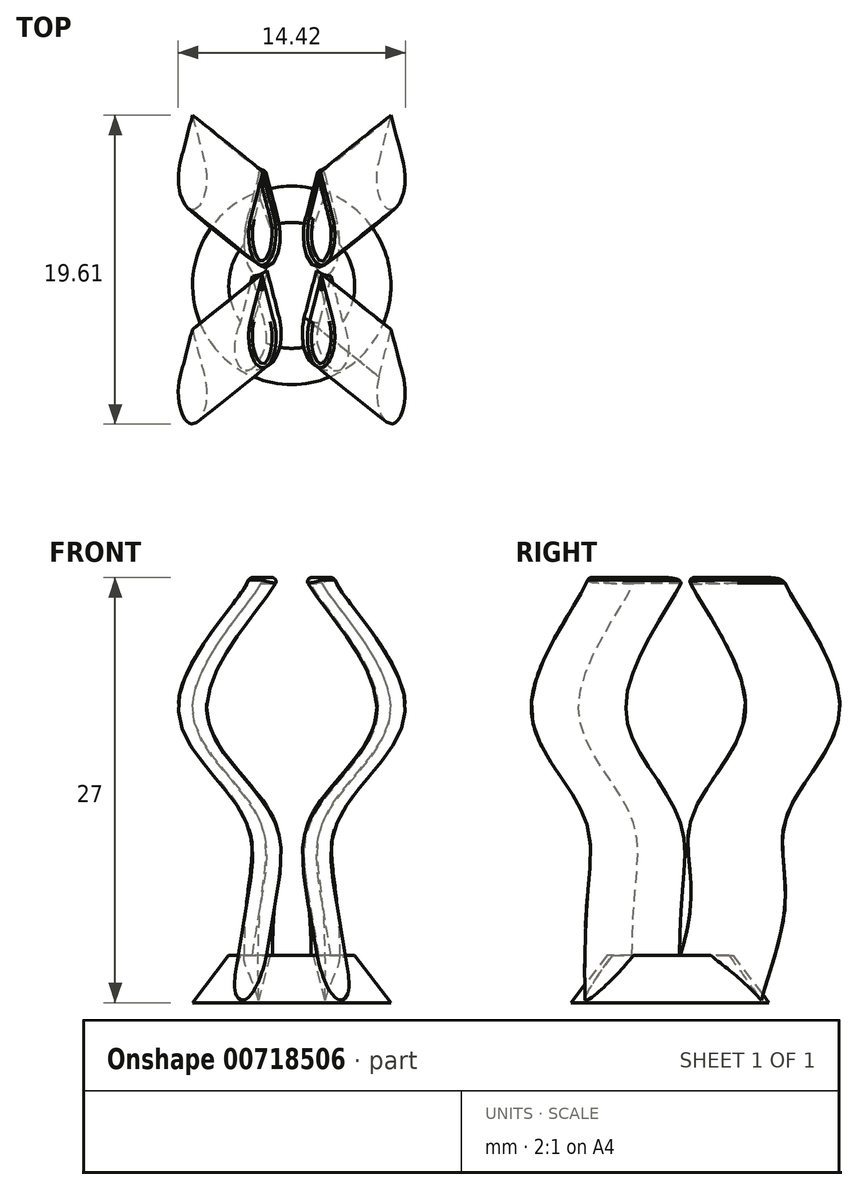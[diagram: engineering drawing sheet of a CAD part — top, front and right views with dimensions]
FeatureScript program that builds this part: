
annotation { "Feature Type Name" : "Feature", "Feature Type Description" : "" }
export const myFeature = defineFeature(function(context is Context, id is Id, definition is map)
    precondition{}
    {
        {
            var Q0;
            Q0=qCreatedBy(makeId("Top.planeOp"),FACE);
            var sketch = newSketch(context, id + "F0", { "sketchPlane" : qUnion([Q0])});
            skCircle(sketch, "E0", {"center": v(0, 0) * mm, "radius": 6.3 * mm});
            skSolve(sketch);
        }
        {
            assignVariable(context, id + "F1", {"variableType" : VariableType.LENGTH, "name" : "BaseHeight", "lengthValue" : 3 * mm});
        }
        {
            var Q0;
            Q0=qCreatedBy(makeId("Top.planeOp"),FACE);
            cPlane(context, id + "F2", {"entities" : qUnion([Q0]), "cplaneType" : CPlaneType.OFFSET, "offset" : getVariable(context, 'BaseHeight'), "width" : 150 * mm, "height" : 150 * mm});
        }
        {
            var Q0;
            Q0=qCreatedBy(id+"F2.planeOp",FACE);
            var sketch = newSketch(context, id + "F3", { "sketchPlane" : qUnion([Q0])});
            skCircle(sketch, "E1", {"center": v(0, 0) * mm, "radius": 4 * mm});
            skSolve(sketch);
        }
        {
            assignVariable(context, id + "F4", {"variableType" : VariableType.LENGTH, "name" : "PostH1", "lengthValue" : 6 * mm});
        }
        {
            assignVariable(context, id + "F5", {"variableType" : VariableType.LENGTH, "name" : "PostH2", "lengthValue" : 11 * mm});
        }
        {
            assignVariable(context, id + "F6", {"variableType" : VariableType.LENGTH, "name" : "PostH3", "lengthValue" : 19 * mm});
        }
        {
            assignVariable(context, id + "F7", {"variableType" : VariableType.LENGTH, "name" : "PostH4", "lengthValue" : 27 * mm});
        }
        {
            var Q0;
            Q0=qCreatedBy(makeId("Top.planeOp"),FACE);
            cPlane(context, id + "F8", {"entities" : qUnion([Q0]), "cplaneType" : CPlaneType.OFFSET, "offset" : getVariable(context, 'PostH1'), "width" : 150 * mm, "height" : 150 * mm});
        }
        {
            var Q0;
            Q0=qCreatedBy(makeId("Top.planeOp"),FACE);
            cPlane(context, id + "F9", {"entities" : qUnion([Q0]), "cplaneType" : CPlaneType.OFFSET, "offset" : getVariable(context, 'PostH2'), "width" : 150 * mm, "height" : 150 * mm});
        }
        {
            var Q0;
            Q0=qCreatedBy(makeId("Top.planeOp"),FACE);
            cPlane(context, id + "F10", {"entities" : qUnion([Q0]), "cplaneType" : CPlaneType.OFFSET, "offset" : getVariable(context, 'PostH3'), "width" : 150 * mm, "height" : 150 * mm});
        }
        {
            var Q0;
            Q0=qCreatedBy(makeId("Top.planeOp"),FACE);
            cPlane(context, id + "F11", {"entities" : qUnion([Q0]), "cplaneType" : CPlaneType.OFFSET, "offset" : getVariable(context, 'PostH4'), "width" : 150 * mm, "height" : 150 * mm});
        }
        {
            var Q0;
            Q0=makeQuery(id+"F0.imprint","IMPRINT",FACE,{"disambiguationData":[TD([[makeQuery(id+"F0.imprint","IMPRINT",EDGE,{"derivedFrom":sQuery(id+"F0.wireOp",EDGE,"E0")}),1.0]])]});
            var Q1;
            Q1=makeQuery(id+"F3.imprint","IMPRINT",FACE,{"disambiguationData":[TD([[makeQuery(id+"F3.imprint","IMPRINT",EDGE,{"derivedFrom":sQuery(id+"F3.wireOp",EDGE,"E1")}),1.0]])]});
            loft(context, id + "F12", {"sheetProfilesArray" : [{ "sheetProfileEntities" : qUnion([Q0]) }, { "sheetProfileEntities" : qUnion([Q1]) }]});
        }
        {
            var Q0;
            Q0=qCreatedBy(makeId("Top.planeOp"),FACE);
            var sketch = newSketch(context, id + "F13", { "sketchPlane" : qUnion([Q0])});
            skEllipse(sketch, "E2", {"center": v(-2.1, 1.8) * mm, "majorRadius": 2 * mm, "minorRadius": 0.9 * mm, "majorAxis": v(0, 1)});
            skLineSegment(sketch, "E3", {"start": v(-2.88, 2.8) * mm, "end": v(-2.1, 5.8) * mm});
            skLineSegment(sketch, "E4", {"start": v(-2.1, 5.8) * mm, "end": v(-1.32, 2.8) * mm});
            skEllipse(sketch, "E5", {"center": v(2.1, 1.8) * mm, "majorRadius": 2 * mm, "minorRadius": 0.9 * mm, "majorAxis": v(0, 1)});
            skLineSegment(sketch, "E6", {"start": v(1.32, 2.8) * mm, "end": v(2.1, 5.8) * mm});
            skLineSegment(sketch, "E7", {"start": v(2.1, 5.8) * mm, "end": v(2.88, 2.8) * mm});
            skEllipse(sketch, "E8", {"center": v(-2.9, -3.4) * mm, "majorRadius": 2 * mm, "minorRadius": 0.9 * mm, "majorAxis": v(0, 1)});
            skLineSegment(sketch, "E9", {"start": v(-3.68, -2.4) * mm, "end": v(-2.9, 0.6) * mm});
            skLineSegment(sketch, "E10", {"start": v(-2.9, 0.6) * mm, "end": v(-2.12, -2.4) * mm});
            skEllipse(sketch, "E11", {"center": v(2.9, -3.4) * mm, "majorRadius": 2 * mm, "minorRadius": 0.9 * mm, "majorAxis": v(0, 1)});
            skLineSegment(sketch, "E12", {"start": v(2.12, -2.4) * mm, "end": v(2.9, 0.6) * mm});
            skLineSegment(sketch, "E13", {"start": v(2.9, 0.6) * mm, "end": v(3.68, -2.4) * mm});
            skSolve(sketch);
        }
        {
            var Q0;
            Q0=qCreatedBy(id+"F8.planeOp",FACE);
            var sketch = newSketch(context, id + "F14", { "sketchPlane" : qUnion([Q0])});
            skEllipse(sketch, "E14", {"center": v(-2, 3.3) * mm, "majorRadius": 2 * mm, "minorRadius": 0.9 * mm, "majorAxis": v(0, 1)});
            skLineSegment(sketch, "E15", {"start": v(-2.78, 4.3) * mm, "end": v(-2, 7.3) * mm});
            skLineSegment(sketch, "E16", {"start": v(-2, 7.3) * mm, "end": v(-1.22, 4.3) * mm});
            skEllipse(sketch, "E17", {"center": v(2, 3.3) * mm, "majorRadius": 2 * mm, "minorRadius": 0.9 * mm, "majorAxis": v(0, 1)});
            skLineSegment(sketch, "E18", {"start": v(1.22, 4.3) * mm, "end": v(2, 7.3) * mm});
            skLineSegment(sketch, "E19", {"start": v(2, 7.3) * mm, "end": v(2.78, 4.3) * mm});
            skEllipse(sketch, "E20", {"center": v(-2, -3.3) * mm, "majorRadius": 2 * mm, "minorRadius": 0.9 * mm, "majorAxis": v(0, 1)});
            skLineSegment(sketch, "E21", {"start": v(-2.78, -2.3) * mm, "end": v(-2, 0.7) * mm});
            skLineSegment(sketch, "E22", {"start": v(-2, 0.7) * mm, "end": v(-1.22, -2.3) * mm});
            skEllipse(sketch, "E23", {"center": v(2, -3.3) * mm, "majorRadius": 2 * mm, "minorRadius": 0.9 * mm, "majorAxis": v(0, 1)});
            skLineSegment(sketch, "E24", {"start": v(1.22, -2.3) * mm, "end": v(2, 0.7) * mm});
            skLineSegment(sketch, "E25", {"start": v(2, 0.7) * mm, "end": v(2.78, -2.3) * mm});
            skSolve(sketch);
        }
        {
            var Q0;
            Q0=qCreatedBy(id+"F9.planeOp",FACE);
            var sketch = newSketch(context, id + "F15", { "sketchPlane" : qUnion([Q0])});
            skEllipse(sketch, "E26", {"center": v(-1.8, 3.2) * mm, "majorRadius": 2 * mm, "minorRadius": 0.9 * mm, "majorAxis": v(0, 1)});
            skLineSegment(sketch, "E27", {"start": v(-2.58, 4.2) * mm, "end": v(-1.8, 7.2) * mm});
            skLineSegment(sketch, "E28", {"start": v(-1.8, 7.2) * mm, "end": v(-1.02, 4.2) * mm});
            skEllipse(sketch, "E29", {"center": v(1.8, 3.2) * mm, "majorRadius": 2 * mm, "minorRadius": 0.9 * mm, "majorAxis": v(0, 1)});
            skLineSegment(sketch, "E30", {"start": v(1.02, 4.2) * mm, "end": v(1.8, 7.2) * mm});
            skLineSegment(sketch, "E31", {"start": v(1.8, 7.2) * mm, "end": v(2.58, 4.2) * mm});
            skEllipse(sketch, "E32", {"center": v(-1.8, -3.2) * mm, "majorRadius": 2 * mm, "minorRadius": 0.9 * mm, "majorAxis": v(0, 1)});
            skLineSegment(sketch, "E33", {"start": v(-2.58, -2.2) * mm, "end": v(-1.8, 0.8) * mm});
            skLineSegment(sketch, "E34", {"start": v(-1.8, 0.8) * mm, "end": v(-1.02, -2.2) * mm});
            skEllipse(sketch, "E35", {"center": v(1.8, -3.2) * mm, "majorRadius": 2 * mm, "minorRadius": 0.9 * mm, "majorAxis": v(0, 1)});
            skLineSegment(sketch, "E36", {"start": v(1.02, -2.2) * mm, "end": v(1.8, 0.8) * mm});
            skLineSegment(sketch, "E37", {"start": v(1.8, 0.8) * mm, "end": v(2.58, -2.2) * mm});
            skSolve(sketch);
        }
        {
            var Q0;
            Q0=qCreatedBy(id+"F10.planeOp",FACE);
            var sketch = newSketch(context, id + "F16", { "sketchPlane" : qUnion([Q0])});
            skEllipse(sketch, "E38", {"center": v(-6.3, 6.8) * mm, "majorRadius": 2 * mm, "minorRadius": 0.9 * mm, "majorAxis": v(0, 1)});
            skLineSegment(sketch, "E39", {"start": v(-7.08, 7.8) * mm, "end": v(-6.3, 10.8) * mm});
            skLineSegment(sketch, "E40", {"start": v(-6.3, 10.8) * mm, "end": v(-5.52, 7.8) * mm});
            skEllipse(sketch, "E41", {"center": v(6.3, 6.8) * mm, "majorRadius": 2 * mm, "minorRadius": 0.9 * mm, "majorAxis": v(0, 1)});
            skLineSegment(sketch, "E42", {"start": v(5.52, 7.8) * mm, "end": v(6.3, 10.8) * mm});
            skLineSegment(sketch, "E43", {"start": v(6.3, 10.8) * mm, "end": v(7.08, 7.8) * mm});
            skEllipse(sketch, "E44", {"center": v(-6.3, -6.8) * mm, "majorRadius": 2 * mm, "minorRadius": 0.9 * mm, "majorAxis": v(0, 1)});
            skLineSegment(sketch, "E45", {"start": v(-7.08, -5.8) * mm, "end": v(-6.3, -2.8) * mm});
            skLineSegment(sketch, "E46", {"start": v(-6.3, -2.8) * mm, "end": v(-5.52, -5.8) * mm});
            skEllipse(sketch, "E47", {"center": v(6.3, -6.8) * mm, "majorRadius": 2 * mm, "minorRadius": 0.9 * mm, "majorAxis": v(0, 1)});
            skLineSegment(sketch, "E48", {"start": v(5.52, -5.8) * mm, "end": v(6.3, -2.8) * mm});
            skLineSegment(sketch, "E49", {"start": v(6.3, -2.8) * mm, "end": v(7.08, -5.8) * mm});
            skSolve(sketch);
        }
        {
            var Q0;
            Q0=qCreatedBy(id+"F11.planeOp",FACE);
            var sketch = newSketch(context, id + "F17", { "sketchPlane" : qUnion([Q0])});
            skEllipse(sketch, "E50", {"center": v(-1.8, 3.2) * mm, "majorRadius": 2 * mm, "minorRadius": 0.9 * mm, "majorAxis": v(0, 1)});
            skLineSegment(sketch, "E51", {"start": v(-2.58, 4.2) * mm, "end": v(-1.8, 7.2) * mm});
            skLineSegment(sketch, "E52", {"start": v(-1.8, 7.2) * mm, "end": v(-1.02, 4.2) * mm});
            skEllipse(sketch, "E53", {"center": v(1.8, 3.2) * mm, "majorRadius": 2 * mm, "minorRadius": 0.9 * mm, "majorAxis": v(0, 1)});
            skLineSegment(sketch, "E54", {"start": v(1.02, 4.2) * mm, "end": v(1.8, 7.2) * mm});
            skLineSegment(sketch, "E55", {"start": v(1.8, 7.2) * mm, "end": v(2.58, 4.2) * mm});
            skEllipse(sketch, "E56", {"center": v(-1.8, -3.2) * mm, "majorRadius": 2 * mm, "minorRadius": 0.9 * mm, "majorAxis": v(0, 1)});
            skLineSegment(sketch, "E57", {"start": v(-2.58, -2.2) * mm, "end": v(-1.8, 0.8) * mm});
            skLineSegment(sketch, "E58", {"start": v(-1.8, 0.8) * mm, "end": v(-1.02, -2.2) * mm});
            skEllipse(sketch, "E59", {"center": v(1.8, -3.2) * mm, "majorRadius": 2 * mm, "minorRadius": 0.9 * mm, "majorAxis": v(0, 1)});
            skLineSegment(sketch, "E60", {"start": v(1.02, -2.2) * mm, "end": v(1.8, 0.8) * mm});
            skLineSegment(sketch, "E61", {"start": v(1.8, 0.8) * mm, "end": v(2.58, -2.2) * mm});
            skSolve(sketch);
        }
        {
            assignVariable(context, id + "F18", {"variableType" : VariableType.NUMBER, "name" : "Loft1", "numberValue" : 0.3});
        }
        {
            var Q0;
            {var subQ0=sQuery(id+"F13.wireOp",EDGE,"E5");var subQ1=makeQuery(id+"F13.imprint","INTERSECT",VERTEX,{"derivedFrom":[subQ0,sQuery(id+"F13.wireOp",EDGE,"E6")]});Q0=makeQuery(id+"F13.imprint","IMPRINT",FACE,{"disambiguationData":[TD([[makeQuery(id+"F13.imprint","IMPRINT",EDGE,{"disambiguationData":[TD([[subQ1,-1.0]])],"derivedFrom":subQ0}),1.0]])]});}
            var Q1;
            {var subQ0=sQuery(id+"F13.wireOp",EDGE,"E6");Q1=makeQuery(id+"F13.imprint","IMPRINT",FACE,{"disambiguationData":[TD([[makeQuery(id+"F13.imprint","IMPRINT",EDGE,{"derivedFrom":subQ0}),-1.0]])]});}
            var Q2;
            {var subQ0=sQuery(id+"F14.wireOp",EDGE,"E17");var subQ1=makeQuery(id+"F14.imprint","INTERSECT",VERTEX,{"derivedFrom":[subQ0,sQuery(id+"F14.wireOp",EDGE,"E18")]});Q2=makeQuery(id+"F14.imprint","IMPRINT",FACE,{"disambiguationData":[TD([[makeQuery(id+"F14.imprint","IMPRINT",EDGE,{"disambiguationData":[TD([[subQ1,-1.0]])],"derivedFrom":subQ0}),1.0]])]});}
            var Q3;
            {var subQ0=sQuery(id+"F14.wireOp",EDGE,"E18");Q3=makeQuery(id+"F14.imprint","IMPRINT",FACE,{"disambiguationData":[TD([[makeQuery(id+"F14.imprint","IMPRINT",EDGE,{"derivedFrom":subQ0}),-1.0]])]});}
            var Q4;
            {var subQ0=sQuery(id+"F15.wireOp",EDGE,"E29");var subQ1=makeQuery(id+"F15.imprint","INTERSECT",VERTEX,{"derivedFrom":[subQ0,sQuery(id+"F15.wireOp",EDGE,"E30")]});Q4=makeQuery(id+"F15.imprint","IMPRINT",FACE,{"disambiguationData":[TD([[makeQuery(id+"F15.imprint","IMPRINT",EDGE,{"disambiguationData":[TD([[subQ1,-1.0]])],"derivedFrom":subQ0}),1.0]])]});}
            var Q5;
            {var subQ0=sQuery(id+"F15.wireOp",EDGE,"E30");Q5=makeQuery(id+"F15.imprint","IMPRINT",FACE,{"disambiguationData":[TD([[makeQuery(id+"F15.imprint","IMPRINT",EDGE,{"derivedFrom":subQ0}),-1.0]])]});}
            var Q6;
            {var subQ0=sQuery(id+"F16.wireOp",EDGE,"E41");var subQ1=makeQuery(id+"F16.imprint","INTERSECT",VERTEX,{"derivedFrom":[subQ0,sQuery(id+"F16.wireOp",EDGE,"E42")]});Q6=makeQuery(id+"F16.imprint","IMPRINT",FACE,{"disambiguationData":[TD([[makeQuery(id+"F16.imprint","IMPRINT",EDGE,{"disambiguationData":[TD([[subQ1,-1.0]])],"derivedFrom":subQ0}),1.0]])]});}
            var Q7;
            {var subQ0=sQuery(id+"F16.wireOp",EDGE,"E42");Q7=makeQuery(id+"F16.imprint","IMPRINT",FACE,{"disambiguationData":[TD([[makeQuery(id+"F16.imprint","IMPRINT",EDGE,{"derivedFrom":subQ0}),-1.0]])]});}
            var Q8;
            {var subQ0=sQuery(id+"F17.wireOp",EDGE,"E53");var subQ1=makeQuery(id+"F17.imprint","INTERSECT",VERTEX,{"derivedFrom":[subQ0,sQuery(id+"F17.wireOp",EDGE,"E54")]});Q8=makeQuery(id+"F17.imprint","IMPRINT",FACE,{"disambiguationData":[TD([[makeQuery(id+"F17.imprint","IMPRINT",EDGE,{"disambiguationData":[TD([[subQ1,-1.0]])],"derivedFrom":subQ0}),1.0]])]});}
            var Q9;
            {var subQ0=sQuery(id+"F17.wireOp",EDGE,"E54");Q9=makeQuery(id+"F17.imprint","IMPRINT",FACE,{"disambiguationData":[TD([[makeQuery(id+"F17.imprint","IMPRINT",EDGE,{"derivedFrom":subQ0}),-1.0]])]});}
            loft(context, id + "F19", {"operationType" : NewBodyOperationType.ADD, "sheetProfilesArray" : [{ "sheetProfileEntities" : qUnion([Q0, Q1]) }, { "sheetProfileEntities" : qUnion([Q2, Q3]) }, { "sheetProfileEntities" : qUnion([Q4, Q5]) }, { "sheetProfileEntities" : qUnion([Q6, Q7]) }, { "sheetProfileEntities" : qUnion([Q8, Q9]) }], "startCondition" : LoftEndDerivativeType.NORMAL_TO_PROFILE, "startMagnitude" : getVariable(context, 'Loft1'), "endCondition" : LoftEndDerivativeType.NORMAL_TO_PROFILE, "endMagnitude" : getVariable(context, 'Loft1')});
        }
        {
            var Q0;
            {var subQ0=sQuery(id+"F13.wireOp",EDGE,"E3");Q0=makeQuery(id+"F13.imprint","IMPRINT",FACE,{"disambiguationData":[TD([[makeQuery(id+"F13.imprint","IMPRINT",EDGE,{"derivedFrom":subQ0}),-1.0]])]});}
            var Q1;
            {var subQ0=sQuery(id+"F13.wireOp",EDGE,"E2");var subQ1=makeQuery(id+"F13.imprint","INTERSECT",VERTEX,{"derivedFrom":[subQ0,sQuery(id+"F13.wireOp",EDGE,"E3")]});Q1=makeQuery(id+"F13.imprint","IMPRINT",FACE,{"disambiguationData":[TD([[makeQuery(id+"F13.imprint","IMPRINT",EDGE,{"disambiguationData":[TD([[subQ1,-1.0]])],"derivedFrom":subQ0}),1.0]])]});}
            var Q2;
            {var subQ0=sQuery(id+"F14.wireOp",EDGE,"E15");Q2=makeQuery(id+"F14.imprint","IMPRINT",FACE,{"disambiguationData":[TD([[makeQuery(id+"F14.imprint","IMPRINT",EDGE,{"derivedFrom":subQ0}),-1.0]])]});}
            var Q3;
            {var subQ0=sQuery(id+"F14.wireOp",EDGE,"E14");var subQ1=makeQuery(id+"F14.imprint","INTERSECT",VERTEX,{"derivedFrom":[subQ0,sQuery(id+"F14.wireOp",EDGE,"E15")]});Q3=makeQuery(id+"F14.imprint","IMPRINT",FACE,{"disambiguationData":[TD([[makeQuery(id+"F14.imprint","IMPRINT",EDGE,{"disambiguationData":[TD([[subQ1,-1.0]])],"derivedFrom":subQ0}),1.0]])]});}
            var Q4;
            {var subQ0=sQuery(id+"F15.wireOp",EDGE,"E26");var subQ1=makeQuery(id+"F15.imprint","INTERSECT",VERTEX,{"derivedFrom":[subQ0,sQuery(id+"F15.wireOp",EDGE,"E27")]});Q4=makeQuery(id+"F15.imprint","IMPRINT",FACE,{"disambiguationData":[TD([[makeQuery(id+"F15.imprint","IMPRINT",EDGE,{"disambiguationData":[TD([[subQ1,-1.0]])],"derivedFrom":subQ0}),1.0]])]});}
            var Q5;
            {var subQ0=sQuery(id+"F15.wireOp",EDGE,"E27");Q5=makeQuery(id+"F15.imprint","IMPRINT",FACE,{"disambiguationData":[TD([[makeQuery(id+"F15.imprint","IMPRINT",EDGE,{"derivedFrom":subQ0}),-1.0]])]});}
            var Q6;
            {var subQ0=sQuery(id+"F16.wireOp",EDGE,"E38");var subQ1=makeQuery(id+"F16.imprint","INTERSECT",VERTEX,{"derivedFrom":[subQ0,sQuery(id+"F16.wireOp",EDGE,"E39")]});Q6=makeQuery(id+"F16.imprint","IMPRINT",FACE,{"disambiguationData":[TD([[makeQuery(id+"F16.imprint","IMPRINT",EDGE,{"disambiguationData":[TD([[subQ1,-1.0]])],"derivedFrom":subQ0}),1.0]])]});}
            var Q7;
            {var subQ0=sQuery(id+"F16.wireOp",EDGE,"E39");Q7=makeQuery(id+"F16.imprint","IMPRINT",FACE,{"disambiguationData":[TD([[makeQuery(id+"F16.imprint","IMPRINT",EDGE,{"derivedFrom":subQ0}),-1.0]])]});}
            var Q8;
            {var subQ0=sQuery(id+"F17.wireOp",EDGE,"E50");var subQ1=makeQuery(id+"F17.imprint","INTERSECT",VERTEX,{"derivedFrom":[subQ0,sQuery(id+"F17.wireOp",EDGE,"E51")]});Q8=makeQuery(id+"F17.imprint","IMPRINT",FACE,{"disambiguationData":[TD([[makeQuery(id+"F17.imprint","IMPRINT",EDGE,{"disambiguationData":[TD([[subQ1,-1.0]])],"derivedFrom":subQ0}),1.0]])]});}
            var Q9;
            {var subQ0=sQuery(id+"F17.wireOp",EDGE,"E51");Q9=makeQuery(id+"F17.imprint","IMPRINT",FACE,{"disambiguationData":[TD([[makeQuery(id+"F17.imprint","IMPRINT",EDGE,{"derivedFrom":subQ0}),-1.0]])]});}
            loft(context, id + "F20", {"operationType" : NewBodyOperationType.ADD, "sheetProfilesArray" : [{ "sheetProfileEntities" : qUnion([Q0, Q1]) }, { "sheetProfileEntities" : qUnion([Q2, Q3]) }, { "sheetProfileEntities" : qUnion([Q4, Q5]) }, { "sheetProfileEntities" : qUnion([Q6, Q7]) }, { "sheetProfileEntities" : qUnion([Q8, Q9]) }], "startCondition" : LoftEndDerivativeType.NORMAL_TO_PROFILE, "startMagnitude" : getVariable(context, 'Loft1'), "endCondition" : LoftEndDerivativeType.NORMAL_TO_PROFILE, "endMagnitude" : getVariable(context, 'Loft1')});
        }
        {
            var Q0;
            {var subQ0=sQuery(id+"F13.wireOp",EDGE,"E9");Q0=makeQuery(id+"F13.imprint","IMPRINT",FACE,{"disambiguationData":[TD([[makeQuery(id+"F13.imprint","IMPRINT",EDGE,{"derivedFrom":subQ0}),-1.0]])]});}
            var Q1;
            {var subQ0=sQuery(id+"F13.wireOp",EDGE,"E8");var subQ1=makeQuery(id+"F13.imprint","INTERSECT",VERTEX,{"derivedFrom":[subQ0,sQuery(id+"F13.wireOp",EDGE,"E9")]});Q1=makeQuery(id+"F13.imprint","IMPRINT",FACE,{"disambiguationData":[TD([[makeQuery(id+"F13.imprint","IMPRINT",EDGE,{"disambiguationData":[TD([[subQ1,-1.0]])],"derivedFrom":subQ0}),1.0]])]});}
            var Q2;
            {var subQ0=sQuery(id+"F14.wireOp",EDGE,"E21");Q2=makeQuery(id+"F14.imprint","IMPRINT",FACE,{"disambiguationData":[TD([[makeQuery(id+"F14.imprint","IMPRINT",EDGE,{"derivedFrom":subQ0}),-1.0]])]});}
            var Q3;
            {var subQ0=sQuery(id+"F14.wireOp",EDGE,"E20");var subQ1=makeQuery(id+"F14.imprint","INTERSECT",VERTEX,{"derivedFrom":[subQ0,sQuery(id+"F14.wireOp",EDGE,"E21")]});Q3=makeQuery(id+"F14.imprint","IMPRINT",FACE,{"disambiguationData":[TD([[makeQuery(id+"F14.imprint","IMPRINT",EDGE,{"disambiguationData":[TD([[subQ1,-1.0]])],"derivedFrom":subQ0}),1.0]])]});}
            var Q4;
            {var subQ0=sQuery(id+"F15.wireOp",EDGE,"E32");var subQ1=makeQuery(id+"F15.imprint","INTERSECT",VERTEX,{"derivedFrom":[subQ0,sQuery(id+"F15.wireOp",EDGE,"E33")]});Q4=makeQuery(id+"F15.imprint","IMPRINT",FACE,{"disambiguationData":[TD([[makeQuery(id+"F15.imprint","IMPRINT",EDGE,{"disambiguationData":[TD([[subQ1,-1.0]])],"derivedFrom":subQ0}),1.0]])]});}
            var Q5;
            {var subQ0=sQuery(id+"F15.wireOp",EDGE,"E33");Q5=makeQuery(id+"F15.imprint","IMPRINT",FACE,{"disambiguationData":[TD([[makeQuery(id+"F15.imprint","IMPRINT",EDGE,{"derivedFrom":subQ0}),-1.0]])]});}
            var Q6;
            {var subQ0=sQuery(id+"F16.wireOp",EDGE,"E44");var subQ1=makeQuery(id+"F16.imprint","INTERSECT",VERTEX,{"derivedFrom":[subQ0,sQuery(id+"F16.wireOp",EDGE,"E45")]});Q6=makeQuery(id+"F16.imprint","IMPRINT",FACE,{"disambiguationData":[TD([[makeQuery(id+"F16.imprint","IMPRINT",EDGE,{"disambiguationData":[TD([[subQ1,-1.0]])],"derivedFrom":subQ0}),1.0]])]});}
            var Q7;
            {var subQ0=sQuery(id+"F16.wireOp",EDGE,"E45");Q7=makeQuery(id+"F16.imprint","IMPRINT",FACE,{"disambiguationData":[TD([[makeQuery(id+"F16.imprint","IMPRINT",EDGE,{"derivedFrom":subQ0}),-1.0]])]});}
            var Q8;
            {var subQ0=sQuery(id+"F17.wireOp",EDGE,"E56");var subQ1=makeQuery(id+"F17.imprint","INTERSECT",VERTEX,{"derivedFrom":[subQ0,sQuery(id+"F17.wireOp",EDGE,"E57")]});Q8=makeQuery(id+"F17.imprint","IMPRINT",FACE,{"disambiguationData":[TD([[makeQuery(id+"F17.imprint","IMPRINT",EDGE,{"disambiguationData":[TD([[subQ1,-1.0]])],"derivedFrom":subQ0}),1.0]])]});}
            var Q9;
            {var subQ0=sQuery(id+"F17.wireOp",EDGE,"E57");Q9=makeQuery(id+"F17.imprint","IMPRINT",FACE,{"disambiguationData":[TD([[makeQuery(id+"F17.imprint","IMPRINT",EDGE,{"derivedFrom":subQ0}),-1.0]])]});}
            loft(context, id + "F21", {"operationType" : NewBodyOperationType.ADD, "sheetProfilesArray" : [{ "sheetProfileEntities" : qUnion([Q0, Q1]) }, { "sheetProfileEntities" : qUnion([Q2, Q3]) }, { "sheetProfileEntities" : qUnion([Q4, Q5]) }, { "sheetProfileEntities" : qUnion([Q6, Q7]) }, { "sheetProfileEntities" : qUnion([Q8, Q9]) }], "startCondition" : LoftEndDerivativeType.NORMAL_TO_PROFILE, "startMagnitude" : getVariable(context, 'Loft1'), "endCondition" : LoftEndDerivativeType.NORMAL_TO_PROFILE, "endMagnitude" : getVariable(context, 'Loft1')});
        }
        {
            var Q0;
            {var subQ0=sQuery(id+"F13.wireOp",EDGE,"E11");var subQ1=makeQuery(id+"F13.imprint","INTERSECT",VERTEX,{"derivedFrom":[subQ0,sQuery(id+"F13.wireOp",EDGE,"E12")]});Q0=makeQuery(id+"F13.imprint","IMPRINT",FACE,{"disambiguationData":[TD([[makeQuery(id+"F13.imprint","IMPRINT",EDGE,{"disambiguationData":[TD([[subQ1,-1.0]])],"derivedFrom":subQ0}),1.0]])]});}
            var Q1;
            {var subQ0=sQuery(id+"F13.wireOp",EDGE,"E12");Q1=makeQuery(id+"F13.imprint","IMPRINT",FACE,{"disambiguationData":[TD([[makeQuery(id+"F13.imprint","IMPRINT",EDGE,{"derivedFrom":subQ0}),-1.0]])]});}
            var Q2;
            {var subQ0=sQuery(id+"F14.wireOp",EDGE,"E23");var subQ1=makeQuery(id+"F14.imprint","INTERSECT",VERTEX,{"derivedFrom":[subQ0,sQuery(id+"F14.wireOp",EDGE,"E24")]});Q2=makeQuery(id+"F14.imprint","IMPRINT",FACE,{"disambiguationData":[TD([[makeQuery(id+"F14.imprint","IMPRINT",EDGE,{"disambiguationData":[TD([[subQ1,-1.0]])],"derivedFrom":subQ0}),1.0]])]});}
            var Q3;
            {var subQ0=sQuery(id+"F14.wireOp",EDGE,"E24");Q3=makeQuery(id+"F14.imprint","IMPRINT",FACE,{"disambiguationData":[TD([[makeQuery(id+"F14.imprint","IMPRINT",EDGE,{"derivedFrom":subQ0}),-1.0]])]});}
            var Q4;
            {var subQ0=sQuery(id+"F15.wireOp",EDGE,"E35");var subQ1=makeQuery(id+"F15.imprint","INTERSECT",VERTEX,{"derivedFrom":[subQ0,sQuery(id+"F15.wireOp",EDGE,"E36")]});Q4=makeQuery(id+"F15.imprint","IMPRINT",FACE,{"disambiguationData":[TD([[makeQuery(id+"F15.imprint","IMPRINT",EDGE,{"disambiguationData":[TD([[subQ1,-1.0]])],"derivedFrom":subQ0}),1.0]])]});}
            var Q5;
            {var subQ0=sQuery(id+"F15.wireOp",EDGE,"E36");Q5=makeQuery(id+"F15.imprint","IMPRINT",FACE,{"disambiguationData":[TD([[makeQuery(id+"F15.imprint","IMPRINT",EDGE,{"derivedFrom":subQ0}),-1.0]])]});}
            var Q6;
            {var subQ0=sQuery(id+"F16.wireOp",EDGE,"E47");var subQ1=makeQuery(id+"F16.imprint","INTERSECT",VERTEX,{"derivedFrom":[subQ0,sQuery(id+"F16.wireOp",EDGE,"E48")]});Q6=makeQuery(id+"F16.imprint","IMPRINT",FACE,{"disambiguationData":[TD([[makeQuery(id+"F16.imprint","IMPRINT",EDGE,{"disambiguationData":[TD([[subQ1,-1.0]])],"derivedFrom":subQ0}),1.0]])]});}
            var Q7;
            {var subQ0=sQuery(id+"F16.wireOp",EDGE,"E48");Q7=makeQuery(id+"F16.imprint","IMPRINT",FACE,{"disambiguationData":[TD([[makeQuery(id+"F16.imprint","IMPRINT",EDGE,{"derivedFrom":subQ0}),-1.0]])]});}
            var Q8;
            {var subQ0=sQuery(id+"F17.wireOp",EDGE,"E59");var subQ1=makeQuery(id+"F17.imprint","INTERSECT",VERTEX,{"derivedFrom":[subQ0,sQuery(id+"F17.wireOp",EDGE,"E60")]});Q8=makeQuery(id+"F17.imprint","IMPRINT",FACE,{"disambiguationData":[TD([[makeQuery(id+"F17.imprint","IMPRINT",EDGE,{"disambiguationData":[TD([[subQ1,-1.0]])],"derivedFrom":subQ0}),1.0]])]});}
            var Q9;
            {var subQ0=sQuery(id+"F17.wireOp",EDGE,"E60");Q9=makeQuery(id+"F17.imprint","IMPRINT",FACE,{"disambiguationData":[TD([[makeQuery(id+"F17.imprint","IMPRINT",EDGE,{"derivedFrom":subQ0}),-1.0]])]});}
            loft(context, id + "F22", {"operationType" : NewBodyOperationType.ADD, "sheetProfilesArray" : [{ "sheetProfileEntities" : qUnion([Q0, Q1]) }, { "sheetProfileEntities" : qUnion([Q2, Q3]) }, { "sheetProfileEntities" : qUnion([Q4, Q5]) }, { "sheetProfileEntities" : qUnion([Q6, Q7]) }, { "sheetProfileEntities" : qUnion([Q8, Q9]) }], "startCondition" : LoftEndDerivativeType.NORMAL_TO_PROFILE, "startMagnitude" : getVariable(context, 'Loft1'), "endCondition" : LoftEndDerivativeType.NORMAL_TO_PROFILE, "endMagnitude" : getVariable(context, 'Loft1')});
        }
        {
            var Q0;
            {var subQ0=sQuery(id+"F17.wireOp",EDGE,"E57");var subQ1=sQuery(id+"F17.wireOp",EDGE,"E56");var subQ2=makeQuery(id+"F17.imprint","INTERSECT",VERTEX,{"derivedFrom":[subQ1,subQ0]});Q0=makeQuery(id+"F21.opLoft","CAP_FACE",FACE,{"disambiguationData":[OSD([makeQuery(id+"F17.imprint","IMPRINT",FACE,{"disambiguationData":[TD([[makeQuery(id+"F17.imprint","IMPRINT",EDGE,{"disambiguationData":[TD([[subQ2,-1.0]])],"derivedFrom":subQ1}),1.0]])]}),makeQuery(id+"F17.imprint","IMPRINT",FACE,{"disambiguationData":[TD([[makeQuery(id+"F17.imprint","IMPRINT",EDGE,{"derivedFrom":subQ0}),-1.0]])]})])],"isStart":true});}
            var Q1;
            {var subQ0=sQuery(id+"F17.wireOp",EDGE,"E51");var subQ1=sQuery(id+"F17.wireOp",EDGE,"E50");var subQ2=makeQuery(id+"F17.imprint","INTERSECT",VERTEX,{"derivedFrom":[subQ1,subQ0]});Q1=makeQuery(id+"F20.opLoft","CAP_FACE",FACE,{"disambiguationData":[OSD([makeQuery(id+"F17.imprint","IMPRINT",FACE,{"disambiguationData":[TD([[makeQuery(id+"F17.imprint","IMPRINT",EDGE,{"disambiguationData":[TD([[subQ2,-1.0]])],"derivedFrom":subQ1}),1.0]])]}),makeQuery(id+"F17.imprint","IMPRINT",FACE,{"disambiguationData":[TD([[makeQuery(id+"F17.imprint","IMPRINT",EDGE,{"derivedFrom":subQ0}),-1.0]])]})])],"isStart":true});}
            var Q2;
            {var subQ0=sQuery(id+"F17.wireOp",EDGE,"E60");var subQ1=sQuery(id+"F17.wireOp",EDGE,"E59");var subQ2=makeQuery(id+"F17.imprint","INTERSECT",VERTEX,{"derivedFrom":[subQ1,subQ0]});Q2=makeQuery(id+"F22.opLoft","CAP_FACE",FACE,{"disambiguationData":[OSD([makeQuery(id+"F17.imprint","IMPRINT",FACE,{"disambiguationData":[TD([[makeQuery(id+"F17.imprint","IMPRINT",EDGE,{"disambiguationData":[TD([[subQ2,-1.0]])],"derivedFrom":subQ1}),1.0]])]}),makeQuery(id+"F17.imprint","IMPRINT",FACE,{"disambiguationData":[TD([[makeQuery(id+"F17.imprint","IMPRINT",EDGE,{"derivedFrom":subQ0}),-1.0]])]})])],"isStart":true});}
            var Q3;
            {var subQ0=sQuery(id+"F17.wireOp",EDGE,"E54");var subQ1=sQuery(id+"F17.wireOp",EDGE,"E53");var subQ2=makeQuery(id+"F17.imprint","INTERSECT",VERTEX,{"derivedFrom":[subQ1,subQ0]});Q3=makeQuery(id+"F19.opLoft","CAP_FACE",FACE,{"disambiguationData":[OSD([makeQuery(id+"F17.imprint","IMPRINT",FACE,{"disambiguationData":[TD([[makeQuery(id+"F17.imprint","IMPRINT",EDGE,{"disambiguationData":[TD([[subQ2,-1.0]])],"derivedFrom":subQ1}),1.0]])]}),makeQuery(id+"F17.imprint","IMPRINT",FACE,{"disambiguationData":[TD([[makeQuery(id+"F17.imprint","IMPRINT",EDGE,{"derivedFrom":subQ0}),-1.0]])]})])],"isStart":true});}
            var Q4;
            Q4=makeQuery(id+"F21.opLoft","MID_CAP_VERTEX",VERTEX,{"disambiguationData":[OSD([sQuery(id+"F17.wireOp",EDGE,"E57"),sQuery(id+"F17.wireOp",EDGE,"E58")])],"capPos":3.0});
            var Q5;
            Q5=makeQuery(id+"F21.opLoft","MID_CAP_VERTEX",VERTEX,{"disambiguationData":[OSD([sQuery(id+"F17.wireOp",EDGE,"E56"),sQuery(id+"F17.wireOp",EDGE,"E57")])],"capPos":3.0});
            var Q6;
            Q6=makeQuery(id+"F21.opLoft","MID_CAP_VERTEX",VERTEX,{"disambiguationData":[OSD([sQuery(id+"F17.wireOp",EDGE,"E56"),sQuery(id+"F17.wireOp",EDGE,"E58")])],"capPos":3.0});
            fillet(context, id + "F23", {"entities" : qUnion([Q0, Q1, Q2, Q3]), "tangentPropagation" : true, "radius" : 0.25 * mm, "defaultsChanged" : true, "vertexSettings" : [{ "vertex" : qUnion([Q4]), "vertexRadius" : { 'value' : try(0.25 * mm), 'expression' : "0.25 mm" }.value, "variableRho" : { 'value' : try(0.5), 'expression' : "0.5" }.value, "variableMagnitude" : { 'value' : try(0.5), 'expression' : "0.5" }.value }, { "vertex" : qUnion([Q5]), "vertexRadius" : { 'value' : try(0.2 * mm), 'expression' : "0.2 mm" }.value, "variableRho" : { 'value' : try(0.5), 'expression' : "0.5" }.value, "variableMagnitude" : { 'value' : try(0.5), 'expression' : "0.5" }.value }, { "vertex" : qUnion([Q6]), "vertexRadius" : { 'value' : try(0.25 * mm), 'expression' : "0.25 mm" }.value, "variableRho" : { 'value' : try(0.5), 'expression' : "0.5" }.value, "variableMagnitude" : { 'value' : try(0.5), 'expression' : "0.5" }.value }]});
        }
    });
